FCSTD DOCUMENT  (FreeCAD 0.20R29177 +426 (Git))
Label: 01-first-design
License: All rights reserved
LicenseURL: http://en.wikipedia.org/wiki/All_rights_reserved
objects: Sketcher::SketchObject×1, PartDesign::Body×1
note: 2 computed .brp shape members not serialized (recipe doc carries the construction recipe); baked Part::Feature solids carry a one-line shape summary decoded from their .brp

FEATURE [Sketcher::SketchObject] Sketch
  FullyConstrained = true
  MapMode = 5
  Placement = pos=(0,0,0) rot=(1,0,0;1.5708rad)
  Support = -> [XZ_Plane]
  sketch-geometry (16):
    g0: Circle CenterX=0 CenterY=0 CenterZ=0 NormalX=0 NormalY=0 NormalZ=1 AngleXU=0 Radius=10
    g1: Circle CenterX=0 CenterY=0 CenterZ=0 NormalX=0 NormalY=0 NormalZ=1 AngleXU=0 Radius=5
    g2: LineSegment StartX=0 StartY=0 StartZ=0 EndX=100 EndY=0 EndZ=0
    g3: Circle CenterX=100 CenterY=0 CenterZ=0 NormalX=0 NormalY=0 NormalZ=1 AngleXU=0 Radius=10
    g4: Circle CenterX=100 CenterY=0 CenterZ=0 NormalX=0 NormalY=0 NormalZ=1 AngleXU=0 Radius=5
    g5: ArcOfCircle CenterX=50 CenterY=0 CenterZ=0 NormalX=0 NormalY=0 NormalZ=1 AngleXU=0 Radius=25 StartAngle=4.4077 EndAngle=5.01708
    g6: LineSegment StartX=-3 StartY=9.53939 StartZ=0 EndX=42.5 EndY=23.8485 EndZ=0
    g7: LineSegment StartX=57.5 StartY=23.8485 StartZ=0 EndX=103 EndY=9.53939 EndZ=0
    g8: LineSegment StartX=-3 StartY=-9.53939 StartZ=0 EndX=42.5 EndY=-23.8485 EndZ=0
    g9: LineSegment StartX=103 StartY=-9.53938 StartZ=0 EndX=57.5 EndY=-23.8485 EndZ=0
    g10: ArcOfCircle CenterX=50 CenterY=0 CenterZ=0 NormalX=0 NormalY=0 NormalZ=1 AngleXU=0 Radius=25 StartAngle=1.2661 EndAngle=1.87549
    g11: ArcOfCircle CenterX=34 CenterY=0 CenterZ=0 NormalX=0 NormalY=0 NormalZ=1 AngleXU=0 Radius=8 StartAngle=1.5708 EndAngle=4.71239
    g12: ArcOfCircle CenterX=66 CenterY=0 CenterZ=0 NormalX=0 NormalY=0 NormalZ=1 AngleXU=0 Radius=8 StartAngle=4.71239 EndAngle=7.85398
    g13: LineSegment StartX=34 StartY=-8 StartZ=0 EndX=66 EndY=-8 EndZ=0
    g14: LineSegment StartX=66 StartY=8 StartZ=0 EndX=34 EndY=8 EndZ=0
    g15: LineSegment StartX=50 StartY=0 StartZ=0 EndX=50 EndY=25 EndZ=0
  constraints (36):
    c: Coincident(g0,g-1)
    c: Coincident(g1,g0)
    c: Diameter(g1) = 10
    c: Diameter(g0) = 20
    c: Coincident(g2,g0)
    c: PointOnObject(g2,g-1)
    c: DistanceX(g2,g2) = 100
    c: Coincident(g3,g2)
    c: Coincident(g4,g3)
    c: Equal(g1,g4)
    c: Equal(g0,g3)
    c: Radius(g5) = 25
    c: Symmetric(g3,g0,g5)
    c: Tangent(g6,g0) = 1.5708
    c: Tangent(g7,g3) = 1.5708
    c: Tangent(g8,g0) = -1.5708
    c: PointOnObject(g9,g3)
    c: Tangent(g9,g3)
    c: Tangent(g5,g8) = -1.5708
    c: Equal(g5,g10)
    c: Tangent(g10,g7) = 1.5708
    c: Coincident(g5,g10)
    c: Tangent(g5,g9) = 1.5708
    c: Tangent(g10,g6) = 1.5708
    c: Tangent(g11,g13) = -1.5708
    c: Tangent(g13,g12) = -1.5708
    c: Tangent(g12,g14) = -1.5708
    c: Tangent(g14,g11) = -1.5708
    c: Equal(g11,g12)
    c: PointOnObject(g11,g2)
    c: Radius(g12) = 8
    c: DistanceX(g11,g12) = 32
    c: Coincident(g15,g5)
    c: PointOnObject(g15,g10)
    c: Vertical(g15)
    c: Symmetric(g11,g12,g5)
FEATURE [PartDesign::Body] Body
  Group = -> [Sketch]
  Origin = -> Origin
